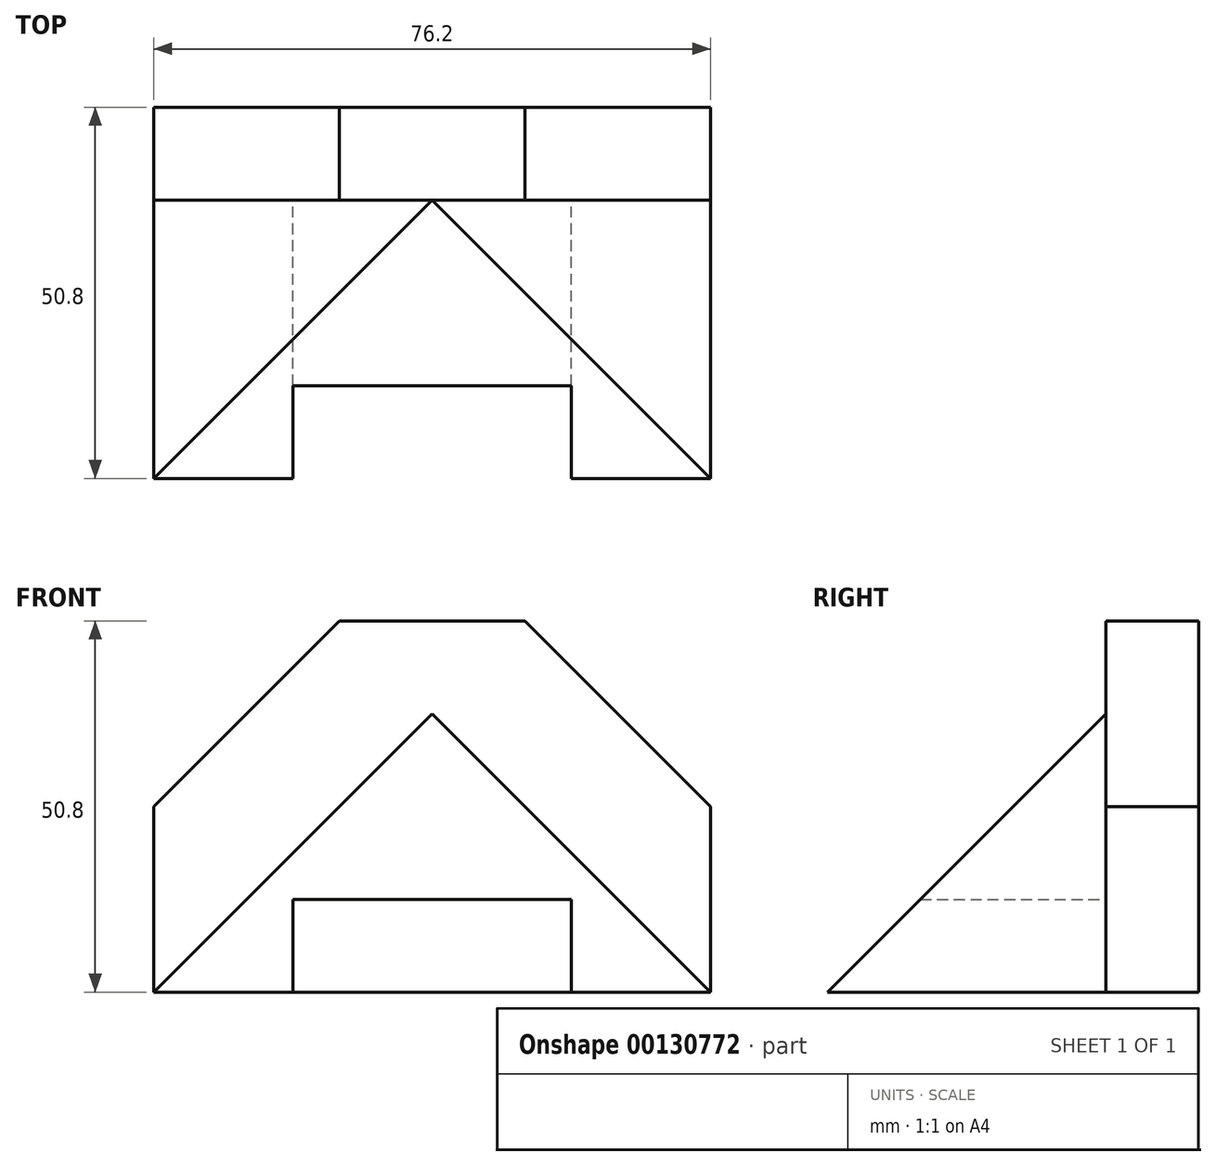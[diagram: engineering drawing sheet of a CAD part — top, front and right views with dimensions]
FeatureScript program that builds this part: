
annotation { "Feature Type Name" : "Feature", "Feature Type Description" : "" }
export const myFeature = defineFeature(function(context is Context, id is Id, definition is map)
    precondition{}
    {
        {
            var Q0;
            Q0=qCreatedBy(makeId("Front.planeOp"),FACE);
            var sketch = newSketch(context, id + "F0", { "sketchPlane" : qUnion([Q0])});
            skLineSegment(sketch, "E0", {"start": v(0, 0) * mm, "end": v(0, 25.4) * mm});
            skLineSegment(sketch, "E1", {"start": v(76.2, 25.4) * mm, "end": v(76.2, 0) * mm});
            skLineSegment(sketch, "E2", {"start": v(76.2, 0) * mm, "end": v(0, 0) * mm});
            skLineSegment(sketch, "E3", {"start": v(0, 25.4) * mm, "end": v(25.4, 50.8) * mm});
            skLineSegment(sketch, "E4", {"start": v(25.4, 50.8) * mm, "end": v(50.8, 50.8) * mm});
            skLineSegment(sketch, "E5", {"start": v(50.8, 50.8) * mm, "end": v(76.2, 25.4) * mm});
            skSolve(sketch);
        }
        {
            var Q0;
            Q0 = qSketchRegion(id + "F0", true);
            extrude(context, id + "F1", {"entities" : qUnion([Q0]), "oppositeDirection" : true, "depth" : 12.7 * mm});
        }
        {
            var Q0;
            Q0=qCreatedBy(makeId("Front.planeOp"),FACE);
            var sketch = newSketch(context, id + "F2", { "sketchPlane" : qUnion([Q0])});
            skLineSegment(sketch, "E6", {"start": v(0, 0) * mm, "end": v(76.2, 0) * mm});
            skLineSegment(sketch, "E7", {"start": v(76.2, 0) * mm, "end": v(38.1, 38.1) * mm});
            skLineSegment(sketch, "E8", {"start": v(38.1, 38.1) * mm, "end": v(0, 0) * mm});
            skSolve(sketch);
        }
        {
            var Q0;
            Q0 = qSketchRegion(id + "F2", true);
            extrude(context, id + "F3", {"entities" : qUnion([Q0]), "operationType" : NewBodyOperationType.ADD, "depth" : 38.1 * mm});
        }
        {
            var Q0;
            Q0=qCreatedBy(makeId("Front.planeOp"),FACE);
            var sketch = newSketch(context, id + "F4", { "sketchPlane" : qUnion([Q0])});
            skLineSegment(sketch, "E9.bottom", {"start": v(19.05, 0) * mm, "end": v(57.15, 0) * mm});
            skLineSegment(sketch, "E9.top", {"start": v(19.05, 12.7) * mm, "end": v(57.15, 12.7) * mm});
            skLineSegment(sketch, "E9.left", {"start": v(19.05, 0) * mm, "end": v(19.05, 12.7) * mm});
            skLineSegment(sketch, "E9.right", {"start": v(57.15, 0) * mm, "end": v(57.15, 12.7) * mm});
            skSolve(sketch);
        }
        {
            var Q0;
            Q0 = qSketchRegion(id + "F4", true);
            extrude(context, id + "F5", {"entities" : qUnion([Q0]), "operationType" : NewBodyOperationType.REMOVE, "endBound" : BoundingType.UP_TO_NEXT, "depth" : 12.7 * mm});
        }
        {
            var Q0;
            Q0=qCreatedBy(makeId("Right.planeOp"),FACE);
            var sketch = newSketch(context, id + "F6", { "sketchPlane" : qUnion([Q0])});
            skLineSegment(sketch, "E10", {"start": v(-38.1, 0) * mm, "end": v(0, 38.1) * mm});
            skLineSegment(sketch, "E11", {"start": v(0, 38.1) * mm, "end": v(-38.1, 38.1) * mm});
            skLineSegment(sketch, "E12", {"start": v(-38.1, 38.1) * mm, "end": v(-38.1, 0) * mm});
            skSolve(sketch);
        }
        {
            var Q0;
            Q0 = qSketchRegion(id + "F6", true);
            extrude(context, id + "F7", {"entities" : qUnion([Q0]), "operationType" : NewBodyOperationType.REMOVE, "endBound" : BoundingType.THROUGH_ALL, "depth" : 25.4 * mm});
        }
    });
